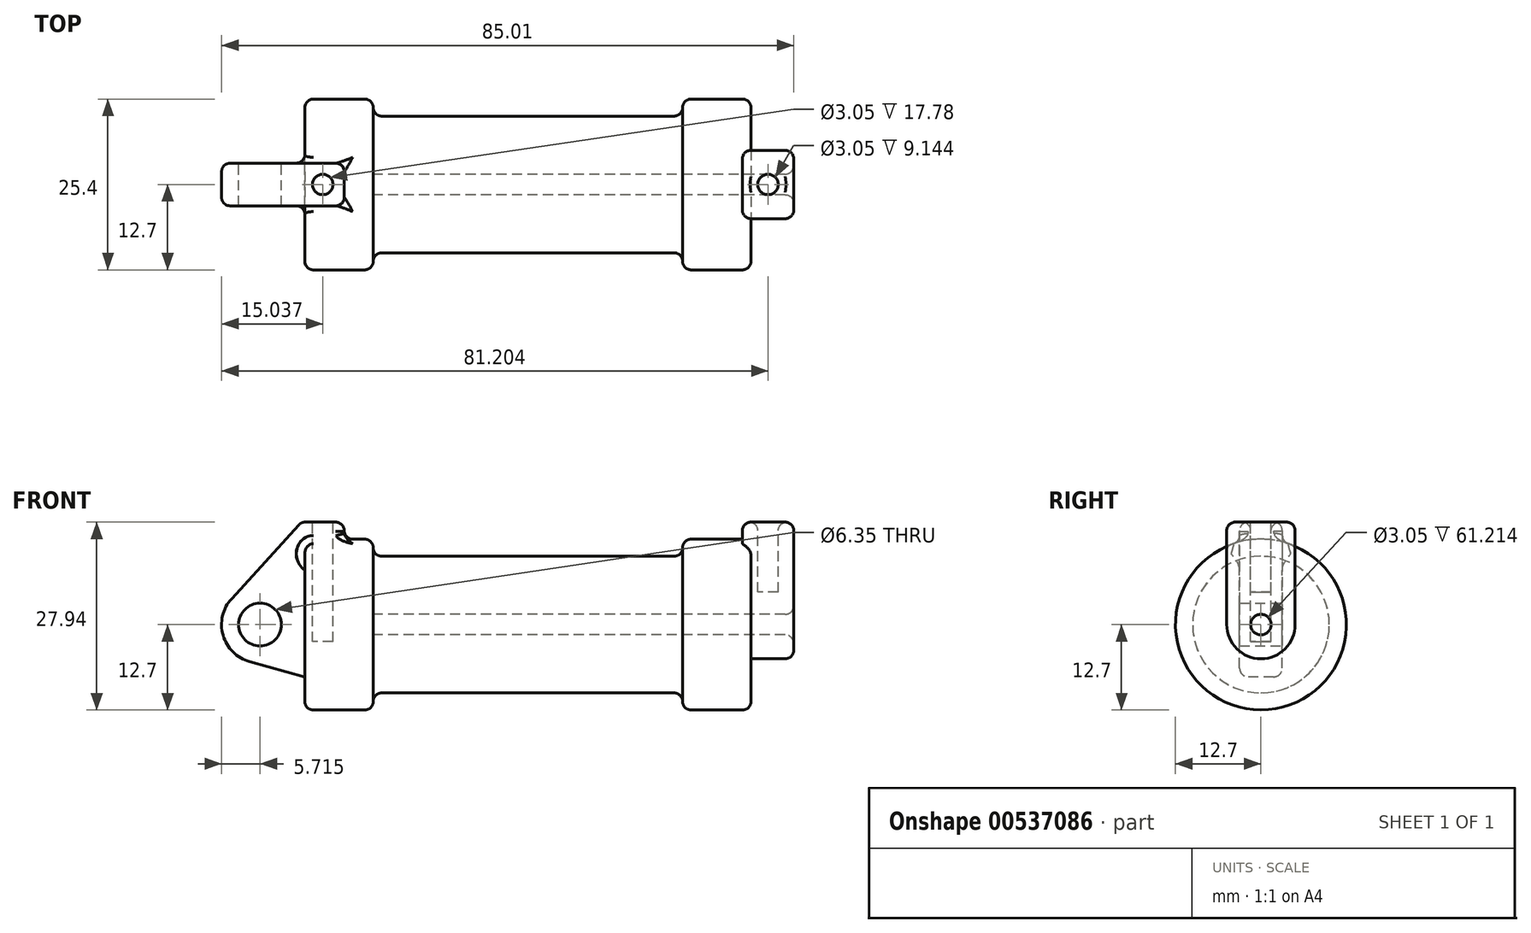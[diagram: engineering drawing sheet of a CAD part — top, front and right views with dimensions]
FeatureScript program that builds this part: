
annotation { "Feature Type Name" : "Feature", "Feature Type Description" : "" }
export const myFeature = defineFeature(function(context is Context, id is Id, definition is map)
    precondition{}
    {
        {
            var Q0;
            Q0=qCreatedBy(makeId("Front.planeOp"),FACE);
            var sketch = newSketch(context, id + "F0", { "sketchPlane" : qUnion([Q0])});
            skLineSegment(sketch, "E0", {"start": v(0, 0) * mm, "end": v(0, 12.7) * mm});
            skLineSegment(sketch, "E1", {"start": v(0, 12.7) * mm, "end": v(10.16, 12.7) * mm});
            skLineSegment(sketch, "E2", {"start": v(10.16, 12.7) * mm, "end": v(10.16, 10.16) * mm});
            skLineSegment(sketch, "E3", {"start": v(10.16, 10.16) * mm, "end": v(56.13, 10.16) * mm});
            skLineSegment(sketch, "E4", {"start": v(56.13, 10.16) * mm, "end": v(56.13, 12.7) * mm});
            skLineSegment(sketch, "E5", {"start": v(56.13, 12.7) * mm, "end": v(66.3, 12.7) * mm});
            skLineSegment(sketch, "E6", {"start": v(66.3, 12.7) * mm, "end": v(66.3, 0) * mm});
            skLineSegment(sketch, "E7", {"start": v(66.3, 0) * mm, "end": v(0, 0) * mm});
            skLineSegment(sketch, "E8", {"start": v(5.84, 15.24) * mm, "end": v(-0.5, 15.24) * mm});
            skLineSegment(sketch, "E9", {"start": v(-0.5, 15.24) * mm, "end": v(-10.88, 3.85) * mm});
            skLineSegment(sketch, "E10", {"start": v(0, 0) * mm, "end": v(-6.65, 0) * mm});
            skCircle(sketch, "E11", {"center": v(-6.65, 0) * mm, "radius": 5.72 * mm});
            skCircle(sketch, "E12", {"center": v(-6.65, 0) * mm, "radius": 3.18 * mm});
            skLineSegment(sketch, "E13", {"start": v(5.84, 15.24) * mm, "end": v(5.84, -9.4) * mm});
            skLineSegment(sketch, "E14", {"start": v(5.84, -9.4) * mm, "end": v(-8.18, -5.5) * mm});
            skSolve(sketch);
        }
        {
            var Q0;
            {var subQ0=sQuery(id+"F0.wireOp",EDGE,"E2");Q0=makeQuery(id+"F0.imprint","IMPRINT",FACE,{"disambiguationData":[TD([[makeQuery(id+"F0.imprint","IMPRINT",EDGE,{"derivedFrom":subQ0}),-1.0]])]});}
            var Q1;
            {var subQ0=sQuery(id+"F0.wireOp",EDGE,"E0");Q1=makeQuery(id+"F0.imprint","IMPRINT",FACE,{"disambiguationData":[TD([[makeQuery(id+"F0.imprint","IMPRINT",EDGE,{"derivedFrom":subQ0}),-1.0]])]});}
            var Q2;
            Q2=sQuery(id+"F0.wireOp",EDGE,"E7");
            revolve(context, id + "F1", {"entities" : qUnion([Q0, Q1]), "axis" : qUnion([Q2]), "revolveType" : RevolveType.FULL});
        }
        {
            var Q0;
            {var subQ5=sQuery(id+"F0.wireOp",EDGE,"E12");Q0=makeQuery(id+"F0.imprint","IMPRINT",FACE,{"disambiguationData":[TD([[makeQuery(id+"F0.imprint","IMPRINT",EDGE,{"derivedFrom":subQ5}),-1.0]])]});}
            var Q1;
            {var subQ0=sQuery(id+"F0.wireOp",EDGE,"E14");Q1=makeQuery(id+"F0.imprint","IMPRINT",FACE,{"disambiguationData":[TD([[makeQuery(id+"F0.imprint","IMPRINT",EDGE,{"derivedFrom":subQ0}),-1.0]])]});}
            var Q2;
            {var subQ1=sQuery(id+"F0.wireOp",EDGE,"E0");Q2=makeQuery(id+"F0.imprint","IMPRINT",FACE,{"disambiguationData":[TD([[makeQuery(id+"F0.imprint","IMPRINT",EDGE,{"derivedFrom":subQ1}),1.0]])]});}
            var Q3;
            {var subQ0=sQuery(id+"F0.wireOp",EDGE,"E0");Q3=makeQuery(id+"F0.imprint","IMPRINT",FACE,{"disambiguationData":[TD([[makeQuery(id+"F0.imprint","IMPRINT",EDGE,{"derivedFrom":subQ0}),-1.0]])]});}
            extrude(context, id + "F2", {"entities" : qUnion([Q0, Q1, Q2, Q3]), "endBound" : BoundingType.SYMMETRIC, "depth" : 6.35 * mm, "offsetDistance" : 25.4 * mm});
        }
        {
            var Q0;
            Q0=makeQuery(id+"F2.opExtrude","SWEPT_BODY",BODY,{"disambiguationData":[OSD([sQuery(id+"F0.wireOp",EDGE,"E8"),sQuery(id+"F0.wireOp",EDGE,"E9"),sQuery(id+"F0.wireOp",EDGE,"E11"),sQuery(id+"F0.wireOp",EDGE,"E12"),sQuery(id+"F0.wireOp",EDGE,"E13"),sQuery(id+"F0.wireOp",EDGE,"E14")])]});
            var Q1;
            Q1=makeQuery(id+"F1.opRevolve","SWEPT_BODY",BODY,{"disambiguationData":[OSD([sQuery(id+"F0.wireOp",EDGE,"E0"),sQuery(id+"F0.wireOp",EDGE,"E1"),sQuery(id+"F0.wireOp",EDGE,"E2"),sQuery(id+"F0.wireOp",EDGE,"E3"),sQuery(id+"F0.wireOp",EDGE,"E4"),sQuery(id+"F0.wireOp",EDGE,"E5"),sQuery(id+"F0.wireOp",EDGE,"E6"),sQuery(id+"F0.wireOp",EDGE,"E7")])]});
            booleanBodies(context, id + "F3", {"operationType" : BooleanOperationType.UNION, "tools" : qUnion([Q0, Q1])});
        }
        {
            var Q0;
            Q0=makeQuery(id+"F1.opRevolve","SWEPT_FACE",FACE,{"disambiguationData":[OSD([sQuery(id+"F0.wireOp",EDGE,"E6")])]});
            var sketch = newSketch(context, id + "F4", { "sketchPlane" : qUnion([Q0])});
            skCircle(sketch, "E15", {"center": v(0, 0) * mm, "radius": 1.52 * mm});
            skCircle(sketch, "E16", {"center": v(0, 0) * mm, "radius": 5.08 * mm});
            skLineSegment(sketch, "E17", {"start": v(-5.08, 0) * mm, "end": v(-5.08, 15.24) * mm});
            skLineSegment(sketch, "E18", {"start": v(-5.08, 15.24) * mm, "end": v(5.08, 15.24) * mm});
            skLineSegment(sketch, "E19", {"start": v(5.08, 15.24) * mm, "end": v(5.08, 0) * mm});
            skSolve(sketch);
        }
        {
            var Q0;
            {var subQ0=sQuery(id+"F4.wireOp",EDGE,"E17");var subQ1=sQuery(id+"F4.wireOp",EDGE,"E16");var subQ2=makeQuery(id+"F4.imprint","INTERSECT",VERTEX,{"derivedFrom":[subQ1,subQ0]});Q0=makeQuery(id+"F4.imprint","IMPRINT",FACE,{"disambiguationData":[TD([[makeQuery(id+"F4.imprint","IMPRINT",EDGE,{"disambiguationData":[TD([[subQ2,1.0]])],"derivedFrom":subQ1}),-1.0]])]});}
            var Q1;
            Q1=makeQuery(id+"F4.imprint","IMPRINT",FACE,{"disambiguationData":[TD([[makeQuery(id+"F4.imprint","IMPRINT",EDGE,{"derivedFrom":sQuery(id+"F4.wireOp",EDGE,"E15")}),-1.0]])]});
            var Q2;
            {var subQ0=sQuery(id+"F4.wireOp",EDGE,"E18");Q2=makeQuery(id+"F4.imprint","IMPRINT",FACE,{"disambiguationData":[TD([[makeQuery(id+"F4.imprint","IMPRINT",EDGE,{"derivedFrom":subQ0}),-1.0]])]});}
            extrude(context, id + "F5", {"entities" : qUnion([Q0, Q1, Q2]), "operationType" : NewBodyOperationType.ADD, "oppositeDirection" : true, "depth" : 1.27 * mm, "offsetDistance" : 25.4 * mm});
        }
        {
            var Q0;
            Q0 = qSketchRegion(id + "F4", true);
            extrude(context, id + "F6", {"entities" : qUnion([Q0]), "operationType" : NewBodyOperationType.ADD, "depth" : 6.35 * mm, "offsetDistance" : 25.4 * mm});
        }
        {
            var Q0;
            {var subQ0=sQuery(id+"F4.wireOp",EDGE,"E15");Q0=makeQuery(id+"F6.boolean.opBoolean","SPLIT",FACE,{"disambiguationData":[TD([makeQuery(id+"F6.opExtrude","SWEPT_FACE",FACE,{"disambiguationData":[OSD([subQ0])]})])],"derivedFrom":makeQuery(id+"F5.boolean.opBoolean","MERGE",FACE,{"derivedFrom":[makeQuery(id+"F1.opRevolve","SWEPT_FACE",FACE,{"disambiguationData":[OSD([sQuery(id+"F0.wireOp",EDGE,"E6")])]}),makeQuery(id+"F5.opExtrude","CAP_FACE",FACE,{"disambiguationData":[OSD([subQ0,sQuery(id+"F4.wireOp",EDGE,"E16"),sQuery(id+"F4.wireOp",EDGE,"E17"),sQuery(id+"F4.wireOp",EDGE,"E18"),sQuery(id+"F4.wireOp",EDGE,"E19")])],"isStart":true})]})});}
            var Q1;
            Q1=makeQuery(id+"F1.opRevolve","SWEPT_FACE",FACE,{"disambiguationData":[OSD([sQuery(id+"F0.wireOp",EDGE,"E2")])]});
            extrude(context, id + "F7", {"entities" : qUnion([Q0]), "operationType" : NewBodyOperationType.REMOVE, "endBound" : BoundingType.UP_TO_SURFACE, "oppositeDirection" : true, "depth" : 50.85 * mm, "endBoundEntityFace" : qUnion([Q1]), "offsetDistance" : 25.4 * mm});
        }
        {
            var Q0;
            {var subQ0=sQuery(id+"F4.wireOp",EDGE,"E18");Q0=makeQuery(id+"F6.boolean.opBoolean","MERGE",FACE,{"derivedFrom":[makeQuery(id+"F5.opExtrude","SWEPT_FACE",FACE,{"disambiguationData":[OSD([subQ0])]}),makeQuery(id+"F6.opExtrude","SWEPT_FACE",FACE,{"disambiguationData":[OSD([subQ0])]})]});}
            var sketch = newSketch(context, id + "F8", { "sketchPlane" : qUnion([Q0])});
            skLineSegment(sketch, "E20", {"start": v(68.83, 5.08) * mm, "end": v(68.83, -5.08) * mm, "construction": true});
            skLineSegment(sketch, "E21", {"start": v(72.64, 0) * mm, "end": v(65.02, 0) * mm, "construction": true});
            skPoint(sketch, "E22", {"position": v(68.83, 0) * mm});
            skCircle(sketch, "E23", {"center": v(68.83, 0) * mm, "radius": 1.52 * mm});
            skSolve(sketch);
        }
        {
            var Q0;
            Q0=makeQuery(id+"F2.opExtrude","SWEPT_FACE",FACE,{"disambiguationData":[OSD([sQuery(id+"F0.wireOp",EDGE,"E8")])]});
            var sketch = newSketch(context, id + "F9", { "sketchPlane" : qUnion([Q0])});
            skLineSegment(sketch, "E24", {"start": v(2.67, 3.18) * mm, "end": v(2.67, -3.18) * mm, "construction": true});
            skLineSegment(sketch, "E25", {"start": v(-0.5, 0) * mm, "end": v(5.84, 0) * mm, "construction": true});
            skPoint(sketch, "E26", {"position": v(2.67, 0) * mm});
            skCircle(sketch, "E27", {"center": v(2.67, 0) * mm, "radius": 1.52 * mm});
            skSolve(sketch);
        }
        {
            var Q0;
            Q0=makeQuery(id+"F9.imprint","IMPRINT",FACE,{"disambiguationData":[TD([[makeQuery(id+"F9.imprint","IMPRINT",EDGE,{"derivedFrom":sQuery(id+"F9.wireOp",EDGE,"E27")}),1.0]])]});
            extrude(context, id + "F10", {"entities" : qUnion([Q0]), "operationType" : NewBodyOperationType.REMOVE, "oppositeDirection" : true, "depth" : 17.78 * mm, "offsetDistance" : 25.4 * mm});
        }
        {
            var Q0;
            Q0=makeQuery(id+"F8.imprint","IMPRINT",FACE,{"disambiguationData":[TD([[makeQuery(id+"F8.imprint","IMPRINT",EDGE,{"derivedFrom":sQuery(id+"F8.wireOp",EDGE,"E23")}),1.0]])]});
            extrude(context, id + "F11", {"entities" : qUnion([Q0]), "operationType" : NewBodyOperationType.REMOVE, "oppositeDirection" : true, "depth" : 10.4 * mm, "offsetDistance" : 25.4 * mm});
        }
        {
            var Q0;
            Q0=makeQuery(id+"F1.opRevolve","SWEPT_FACE",FACE,{"disambiguationData":[OSD([sQuery(id+"F0.wireOp",EDGE,"E3")])]});
            var Q1;
            Q1=makeQuery(id+"F1.opRevolve","SWEPT_EDGE",EDGE,{"disambiguationData":[OSD([sQuery(id+"F0.wireOp",EDGE,"E1"),sQuery(id+"F0.wireOp",EDGE,"E2")])]});
            var Q2;
            Q2=makeQuery(id+"F1.opRevolve","SWEPT_FACE",FACE,{"disambiguationData":[OSD([sQuery(id+"F0.wireOp",EDGE,"E1")])]});
            var Q3;
            Q3=makeQuery(id+"F1.opRevolve","SWEPT_EDGE",EDGE,{"disambiguationData":[OSD([sQuery(id+"F0.wireOp",EDGE,"E4"),sQuery(id+"F0.wireOp",EDGE,"E5")])]});
            var Q4;
            Q4=makeQuery(id+"F1.opRevolve","SWEPT_EDGE",EDGE,{"disambiguationData":[OSD([sQuery(id+"F0.wireOp",EDGE,"E5"),sQuery(id+"F0.wireOp",EDGE,"E6")])]});
            fillet(context, id + "F12", {"entities" : qUnion([Q0, Q1, Q2, Q3, Q4]), "radius" : 1.27 * mm, "tangentPropagation" : true, "allowEdgeOverflow" : false});
        }
        {
            var Q0;
            Q0=makeQuery(id+"F6.opExtrude","CAP_FACE",FACE,{"disambiguationData":[OSD([sQuery(id+"F4.wireOp",EDGE,"E15"),sQuery(id+"F4.wireOp",EDGE,"E16"),sQuery(id+"F4.wireOp",EDGE,"E17"),sQuery(id+"F4.wireOp",EDGE,"E18"),sQuery(id+"F4.wireOp",EDGE,"E19")])],"isStart":false});
            var Q1;
            {var subQ0=sQuery(id+"F4.wireOp",EDGE,"E18");Q1=makeQuery(id+"F6.boolean.opBoolean","MERGE",FACE,{"derivedFrom":[makeQuery(id+"F5.opExtrude","SWEPT_FACE",FACE,{"disambiguationData":[OSD([subQ0])]}),makeQuery(id+"F6.opExtrude","SWEPT_FACE",FACE,{"disambiguationData":[OSD([subQ0])]})]});}
            var Q2;
            Q2=makeQuery(id+"F2.opExtrude","SWEPT_EDGE",EDGE,{"disambiguationData":[OSD([sQuery(id+"F0.wireOp",EDGE,"E8"),sQuery(id+"F0.wireOp",EDGE,"E13")])]});
            var Q3;
            Q3=makeQuery(id+"F2.opExtrude","CAP_EDGE",EDGE,{"disambiguationData":[OSD([sQuery(id+"F0.wireOp",EDGE,"E8")])],"isStart":false});
            var Q4;
            Q4=makeQuery(id+"F2.opExtrude","CAP_EDGE",EDGE,{"disambiguationData":[OSD([sQuery(id+"F0.wireOp",EDGE,"E13")])],"isStart":false});
            var Q5;
            Q5=makeQuery(id+"F2.opExtrude","CAP_EDGE",EDGE,{"disambiguationData":[OSD([sQuery(id+"F0.wireOp",EDGE,"E8")])],"isStart":true});
            var Q6;
            Q6=makeQuery(id+"F2.opExtrude","CAP_EDGE",EDGE,{"disambiguationData":[OSD([sQuery(id+"F0.wireOp",EDGE,"E9")])],"isStart":true});
            var Q7;
            Q7=makeQuery(id+"F2.opExtrude","CAP_EDGE",EDGE,{"disambiguationData":[OSD([sQuery(id+"F0.wireOp",EDGE,"E9")])],"isStart":false});
            var Q8;
            Q8=makeQuery(id+"F2.opExtrude","SWEPT_EDGE",EDGE,{"disambiguationData":[OSD([sQuery(id+"F0.wireOp",EDGE,"E8"),sQuery(id+"F0.wireOp",EDGE,"E9")])]});
            var Q9;
            Q9=makeQuery(id+"F5.opExtrude","CAP_EDGE",EDGE,{"disambiguationData":[OSD([sQuery(id+"F4.wireOp",EDGE,"E19")])],"isStart":false});
            var Q10;
            Q10=makeQuery(id+"F5.opExtrude","CAP_EDGE",EDGE,{"disambiguationData":[OSD([sQuery(id+"F4.wireOp",EDGE,"E17")])],"isStart":false});
            var Q11;
            Q11=makeQuery(id+"F2.opExtrude","CAP_EDGE",EDGE,{"disambiguationData":[OSD([sQuery(id+"F0.wireOp",EDGE,"E13")])],"isStart":true});
            var Q12;
            {var subQ0=makeQuery(id+"F1.opRevolve","SWEPT_FACE",FACE,{"disambiguationData":[OSD([sQuery(id+"F0.wireOp",EDGE,"E1")])]});Q12=makeQuery(id+"F12.opFillet","BLEND_EDGE",EDGE,{"blendedFrom":[makeQuery(id+"F3.opBoolean","INTERSECT",EDGE,{"derivedFrom":[subQ0,makeQuery(id+"F2.opExtrude","CAP_FACE",FACE,{"disambiguationData":[OSD([sQuery(id+"F0.wireOp",EDGE,"E8"),sQuery(id+"F0.wireOp",EDGE,"E9"),sQuery(id+"F0.wireOp",EDGE,"E11"),sQuery(id+"F0.wireOp",EDGE,"E12"),sQuery(id+"F0.wireOp",EDGE,"E13"),sQuery(id+"F0.wireOp",EDGE,"E14")])],"isStart":true})]}),subQ0],"blendedInto":[subQ0]});}
            var Q13;
            {var subQ0=makeQuery(id+"F1.opRevolve","SWEPT_FACE",FACE,{"disambiguationData":[OSD([sQuery(id+"F0.wireOp",EDGE,"E1")])]});Q13=makeQuery(id+"F12.opFillet","BLEND_EDGE",EDGE,{"blendedFrom":[makeQuery(id+"F3.opBoolean","INTERSECT",EDGE,{"derivedFrom":[subQ0,makeQuery(id+"F2.opExtrude","SWEPT_FACE",FACE,{"disambiguationData":[OSD([sQuery(id+"F0.wireOp",EDGE,"E13")])]})]}),subQ0],"blendedInto":[subQ0]});}
            var Q14;
            {var subQ0=sQuery(id+"F0.wireOp",EDGE,"E13");var subQ1=makeQuery(id+"F1.opRevolve","SWEPT_FACE",FACE,{"disambiguationData":[OSD([sQuery(id+"F0.wireOp",EDGE,"E1")])]});Q14=makeQuery(id+"F12.opFillet","BLEND_EDGE",EDGE,{"blendedFrom":[makeQuery(id+"F3.opBoolean","INTERSECT",EDGE,{"derivedFrom":[subQ1,makeQuery(id+"F2.opExtrude","CAP_FACE",FACE,{"disambiguationData":[OSD([sQuery(id+"F0.wireOp",EDGE,"E8"),sQuery(id+"F0.wireOp",EDGE,"E9"),sQuery(id+"F0.wireOp",EDGE,"E11"),sQuery(id+"F0.wireOp",EDGE,"E12"),subQ0,sQuery(id+"F0.wireOp",EDGE,"E14")])],"isStart":true})]}),makeQuery(id+"F3.opBoolean","INTERSECT",EDGE,{"derivedFrom":[subQ1,makeQuery(id+"F2.opExtrude","SWEPT_FACE",FACE,{"disambiguationData":[OSD([subQ0])]})]})],"blendedInto":[]});}
            var Q15;
            {var subQ0=sQuery(id+"F0.wireOp",EDGE,"E13");var subQ1=makeQuery(id+"F1.opRevolve","SWEPT_FACE",FACE,{"disambiguationData":[OSD([sQuery(id+"F0.wireOp",EDGE,"E1")])]});Q15=makeQuery(id+"F12.opFillet","BLEND_EDGE",EDGE,{"blendedFrom":[makeQuery(id+"F3.opBoolean","INTERSECT",EDGE,{"derivedFrom":[subQ1,makeQuery(id+"F2.opExtrude","CAP_FACE",FACE,{"disambiguationData":[OSD([sQuery(id+"F0.wireOp",EDGE,"E8"),sQuery(id+"F0.wireOp",EDGE,"E9"),sQuery(id+"F0.wireOp",EDGE,"E11"),sQuery(id+"F0.wireOp",EDGE,"E12"),subQ0,sQuery(id+"F0.wireOp",EDGE,"E14")])],"isStart":false})]}),makeQuery(id+"F3.opBoolean","INTERSECT",EDGE,{"derivedFrom":[subQ1,makeQuery(id+"F2.opExtrude","SWEPT_FACE",FACE,{"disambiguationData":[OSD([subQ0])]})]})],"blendedInto":[]});}
            fillet(context, id + "F13", {"entities" : qUnion([Q0, Q1, Q2, Q3, Q4, Q5, Q6, Q7, Q8, Q9, Q10, Q11, Q12, Q13, Q14, Q15]), "radius" : 1.27 * mm, "tangentPropagation" : true, "allowEdgeOverflow" : false});
        }
    });
